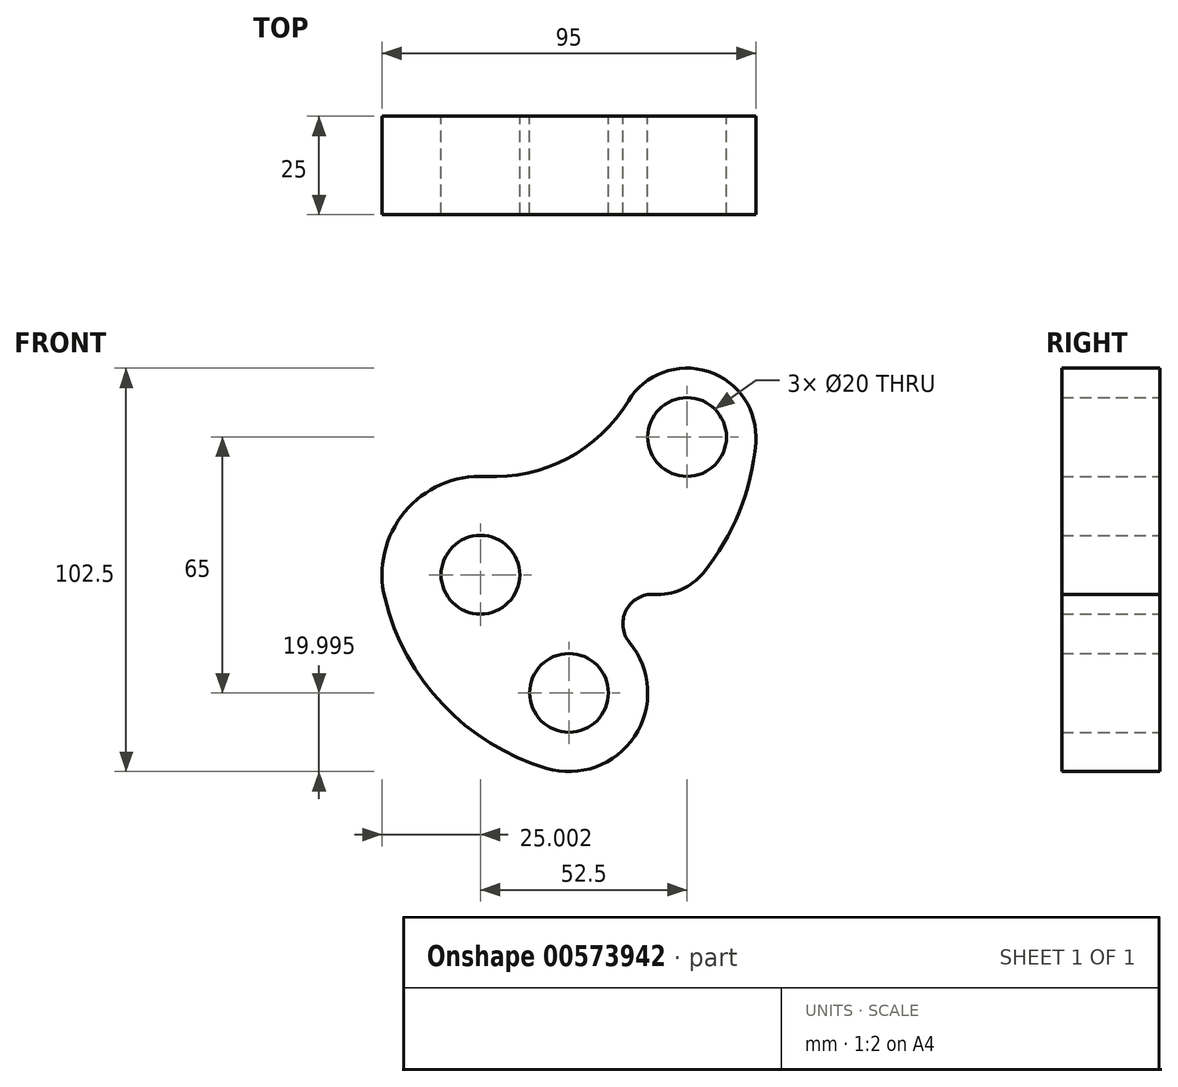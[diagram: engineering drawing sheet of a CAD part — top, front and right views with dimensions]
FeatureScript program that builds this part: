
annotation { "Feature Type Name" : "Feature", "Feature Type Description" : "" }
export const myFeature = defineFeature(function(context is Context, id is Id, definition is map)
    precondition{}
    {
        {
            var Q0;
            Q0=qCreatedBy(makeId("Front.planeOp"),FACE);
            var sketch = newSketch(context, id + "F0", { "sketchPlane" : qUnion([Q0])});
            skCircle(sketch, "E0", {"center": v(-25.38, -5.46) * mm, "radius": 10 * mm});
            skCircle(sketch, "E1", {"center": v(27.12, 29.54) * mm, "radius": 10 * mm});
            skCircle(sketch, "E2", {"center": v(-2.88, -35.46) * mm, "radius": 10 * mm});
            skArc(sketch, "E3", {"start": v(-24.07, 19.5) * mm, "mid": v(-44.63, 10.48) * mm, "end": v(-49.66, -11.4) * mm});
            skArc(sketch, "E4", {"start": v(-8.63, -54.62) * mm, "mid": v(13.8, -46.52) * mm, "end": v(12.53, -22.7) * mm});
            skArc(sketch, "E5", {"start": v(44.56, 28.11) * mm, "mid": v(32.53, 46.18) * mm, "end": v(12.18, 38.64) * mm});
            skArc(sketch, "E6", {"start": v(-24.07, 19.5) * mm, "mid": v(-3.31, 24.07) * mm, "end": v(12.18, 38.64) * mm});
            skArc(sketch, "E7", {"start": v(-49.66, -11.4) * mm, "mid": v(-34.9, -38.47) * mm, "end": v(-8.63, -54.62) * mm});
            skArc(sketch, "E8", {"start": v(18.74, -10.44) * mm, "mid": v(25.65, -9.2) * mm, "end": v(31.24, -4.95) * mm});
            skArc(sketch, "E9", {"start": v(31.24, -4.95) * mm, "mid": v(40.41, 10.57) * mm, "end": v(44.56, 28.11) * mm});
            skArc(sketch, "E10", {"start": v(18.74, -10.44) * mm, "mid": v(11.61, -14.54) * mm, "end": v(12.53, -22.7) * mm});
            skSolve(sketch);
        }
        {
            var Q0;
            Q0=makeQuery(id+"F0.imprint","IMPRINT",FACE,{"disambiguationData":[TD([[makeQuery(id+"F0.imprint","IMPRINT",EDGE,{"derivedFrom":sQuery(id+"F0.wireOp",EDGE,"E0")}),-1.0]])]});
            extrude(context, id + "F1", {"entities" : qUnion([Q0]), "depth" : 25 * mm, "offsetDistance" : 25 * mm});
        }
    });
